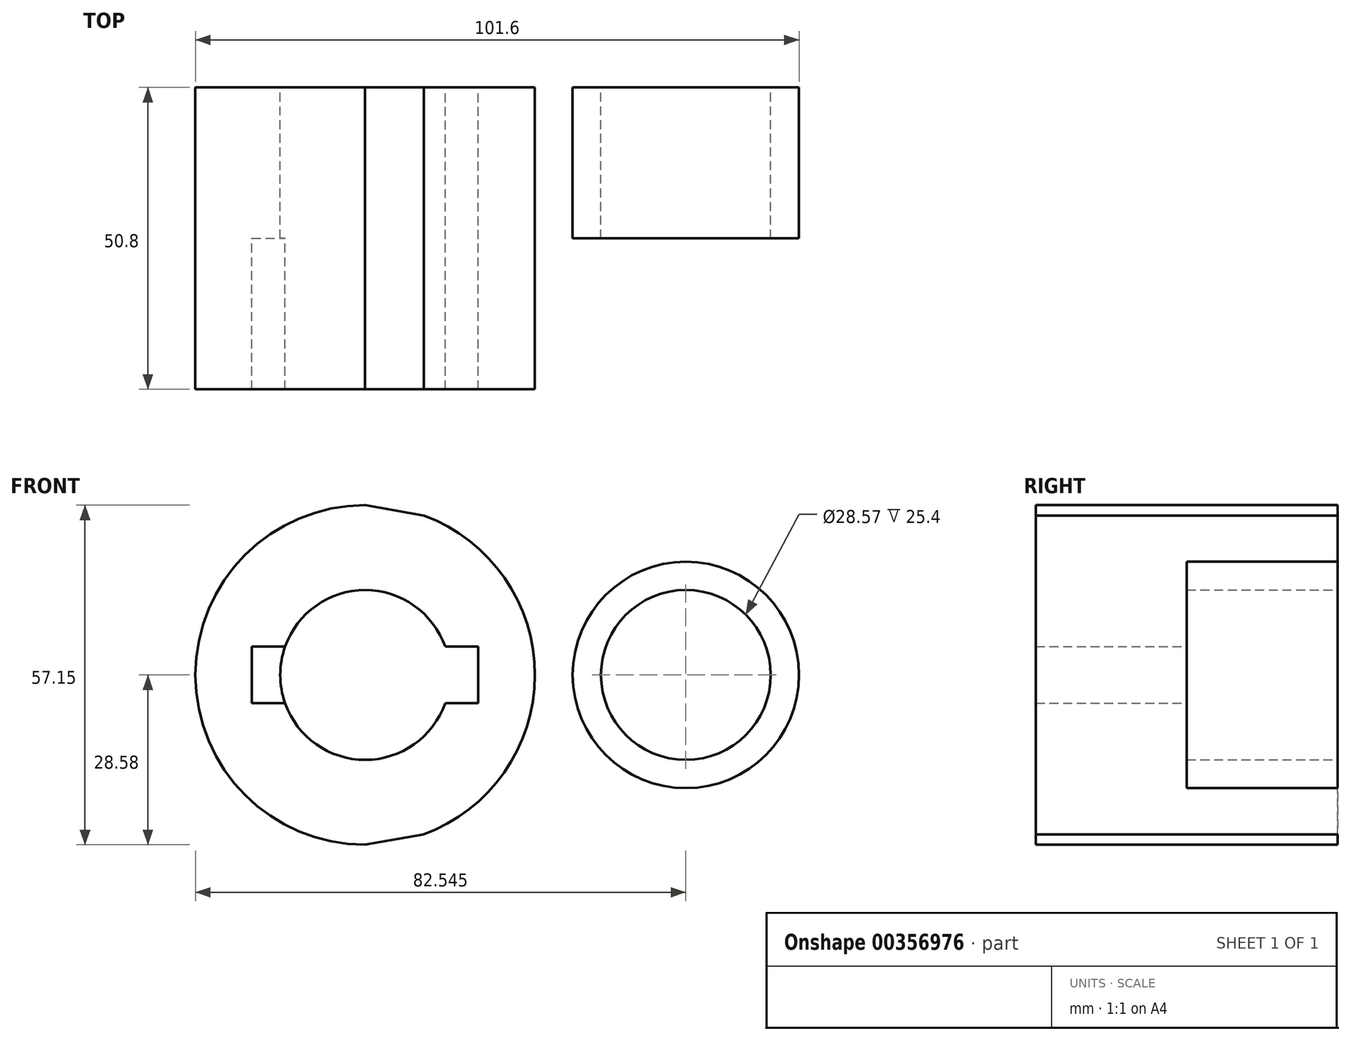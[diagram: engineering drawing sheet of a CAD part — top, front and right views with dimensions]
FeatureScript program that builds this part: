
annotation { "Feature Type Name" : "Feature", "Feature Type Description" : "" }
export const myFeature = defineFeature(function(context is Context, id is Id, definition is map)
    precondition{}
    {
        {
            var Q0;
            Q0=qCreatedBy(makeId("Front.planeOp"),FACE);
            var sketch = newSketch(context, id + "F0", { "sketchPlane" : qUnion([Q0])});
            skCircle(sketch, "E0", {"center": v(0, 0) * mm, "radius": 28.58 * mm});
            skCircle(sketch, "E1", {"center": v(53.98, 0) * mm, "radius": 19.05 * mm});
            skLineSegment(sketch, "E2", {"start": v(0, 28.58) * mm, "end": v(53.41, 19.04) * mm});
            skLineSegment(sketch, "E3", {"start": v(0, -28.58) * mm, "end": v(53.93, -19.05) * mm});
            skCircle(sketch, "E4", {"center": v(0, 0) * mm, "radius": 14.29 * mm});
            skCircle(sketch, "E5", {"center": v(53.98, 0) * mm, "radius": 14.29 * mm});
            skLineSegment(sketch, "E6.bottom", {"start": v(19.05, -4.76) * mm, "end": v(-19.05, -4.76) * mm});
            skLineSegment(sketch, "E6.top", {"start": v(19.05, 4.76) * mm, "end": v(-19.05, 4.76) * mm});
            skLineSegment(sketch, "E6.left", {"start": v(19.05, -4.76) * mm, "end": v(19.05, 4.76) * mm});
            skLineSegment(sketch, "E6.right", {"start": v(-19.05, -4.76) * mm, "end": v(-19.05, 4.76) * mm});
            skSolve(sketch);
        }
        {
            var Q0;
            {var subQ4=sQuery(id+"F0.wireOp",EDGE,"E6.left");Q0=makeQuery(id+"F0.imprint","IMPRINT",FACE,{"disambiguationData":[TD([[makeQuery(id+"F0.imprint","IMPRINT",EDGE,{"derivedFrom":subQ4}),-1.0]])]});}
            var Q1;
            {var subQ0=sQuery(id+"F0.wireOp",EDGE,"E2");var subQ1=sQuery(id+"F0.wireOp",EDGE,"E0");var subQ2=makeQuery(id+"F0.imprint","INTERSECT",VERTEX,{"disambiguationData":[OD(1.0)],"derivedFrom":[subQ1,subQ0]});Q1=makeQuery(id+"F0.imprint","IMPRINT",FACE,{"disambiguationData":[TD([[makeQuery(id+"F0.imprint","IMPRINT",EDGE,{"disambiguationData":[TD([[subQ2,1.0]])],"derivedFrom":subQ1}),-1.0]])]});}
            var Q2;
            Q2=makeQuery(id+"F0.imprint","IMPRINT",FACE,{"disambiguationData":[TD([[makeQuery(id+"F0.imprint","IMPRINT",EDGE,{"derivedFrom":sQuery(id+"F0.wireOp",EDGE,"E5")}),-1.0]])]});
            var Q3;
            {var subQ5=sQuery(id+"F0.wireOp",EDGE,"E6.right");Q3=makeQuery(id+"F0.imprint","IMPRINT",FACE,{"disambiguationData":[TD([[makeQuery(id+"F0.imprint","IMPRINT",EDGE,{"derivedFrom":subQ5}),-1.0]])]});}
            extrude(context, id + "F1", {"entities" : qUnion([Q0, Q1, Q2, Q3]), "depth" : 25.4 * mm});
        }
        {
            var Q0;
            {var subQ4=sQuery(id+"F0.wireOp",EDGE,"E6.left");Q0=makeQuery(id+"F0.imprint","IMPRINT",FACE,{"disambiguationData":[TD([[makeQuery(id+"F0.imprint","IMPRINT",EDGE,{"derivedFrom":subQ4}),-1.0]])]});}
            extrude(context, id + "F2", {"entities" : qUnion([Q0]), "operationType" : NewBodyOperationType.ADD, "depth" : 50.8 * mm});
        }
    });
